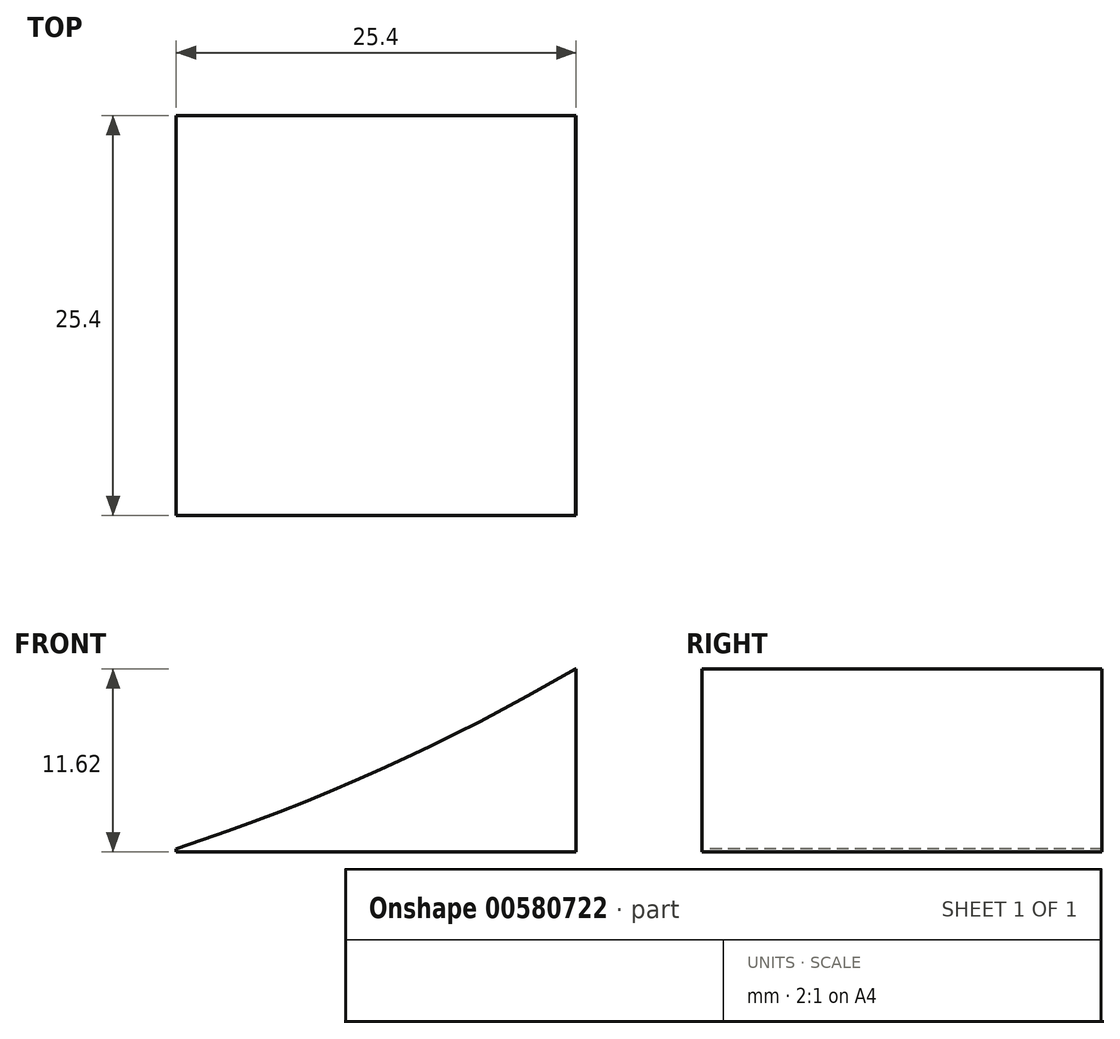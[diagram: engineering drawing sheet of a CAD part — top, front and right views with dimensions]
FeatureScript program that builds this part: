
annotation { "Feature Type Name" : "Feature", "Feature Type Description" : "" }
export const myFeature = defineFeature(function(context is Context, id is Id, definition is map)
    precondition{}
    {
        {
            var Q0;
            Q0=qCreatedBy(makeId("Front.planeOp"),FACE);
            var sketch = newSketch(context, id + "F0", { "sketchPlane" : qUnion([Q0])});
            skLineSegment(sketch, "E0.bottom", {"start": v(12.7, -5.81) * mm, "end": v(-12.7, -5.81) * mm});
            skLineSegment(sketch, "E0.top", {"start": v(12.7, 5.81) * mm, "end": v(-12.7, 5.81) * mm});
            skLineSegment(sketch, "E0.left", {"start": v(12.7, -5.81) * mm, "end": v(12.7, 5.81) * mm});
            skLineSegment(sketch, "E0.right", {"start": v(-12.7, -5.81) * mm, "end": v(-12.7, 5.81) * mm});
            skPoint(sketch, "E0.middle", {"position": v(0, 0) * mm});
            skSolve(sketch);
        }
        {
            var Q0;
            Q0 = qSketchRegion(id + "F0", true);
            extrude(context, id + "F1", {"entities" : qUnion([Q0]), "depth" : 25.4 * mm, "offsetDistance" : 25.4 * mm});
        }
        {
            var Q0;
            Q0=makeQuery(id+"F1.opExtrude","CAP_FACE",FACE,{"disambiguationData":[OSD([sQuery(id+"F0.wireOp",EDGE,"E0.bottom"),sQuery(id+"F0.wireOp",EDGE,"E0.top"),sQuery(id+"F0.wireOp",EDGE,"E0.left"),sQuery(id+"F0.wireOp",EDGE,"E0.right")])],"isStart":false});
            var sketch = newSketch(context, id + "F2", { "sketchPlane" : qUnion([Q0])});
            skCircle(sketch, "E1", {"center": v(-54.22, 120.4) * mm, "radius": 132.67 * mm});
            skSolve(sketch);
        }
        {
            var Q0;
            {var subQ0=sQuery(id+"F2.wireOp",EDGE,"E1");var subQ1=makeQuery(id+"F1.opExtrude","CAP_EDGE",EDGE,{"disambiguationData":[OSD([sQuery(id+"F0.wireOp",EDGE,"E0.top")])],"isStart":false});var subQ2=makeQuery(id+"F2.imprint","INTERSECT",VERTEX,{"derivedFrom":[subQ1,subQ0]});Q0=makeQuery(id+"F2.imprint","IMPRINT",FACE,{"disambiguationData":[TD([[makeQuery(id+"F2.imprint","IMPRINT",EDGE,{"disambiguationData":[TD([[subQ2,1.0]])],"derivedFrom":subQ0}),1.0]])]});}
            extrude(context, id + "F3", {"entities" : qUnion([Q0]), "operationType" : NewBodyOperationType.REMOVE, "endBound" : BoundingType.THROUGH_ALL, "oppositeDirection" : true, "depth" : 25.4 * mm, "offsetDistance" : 25.4 * mm});
        }
    });
